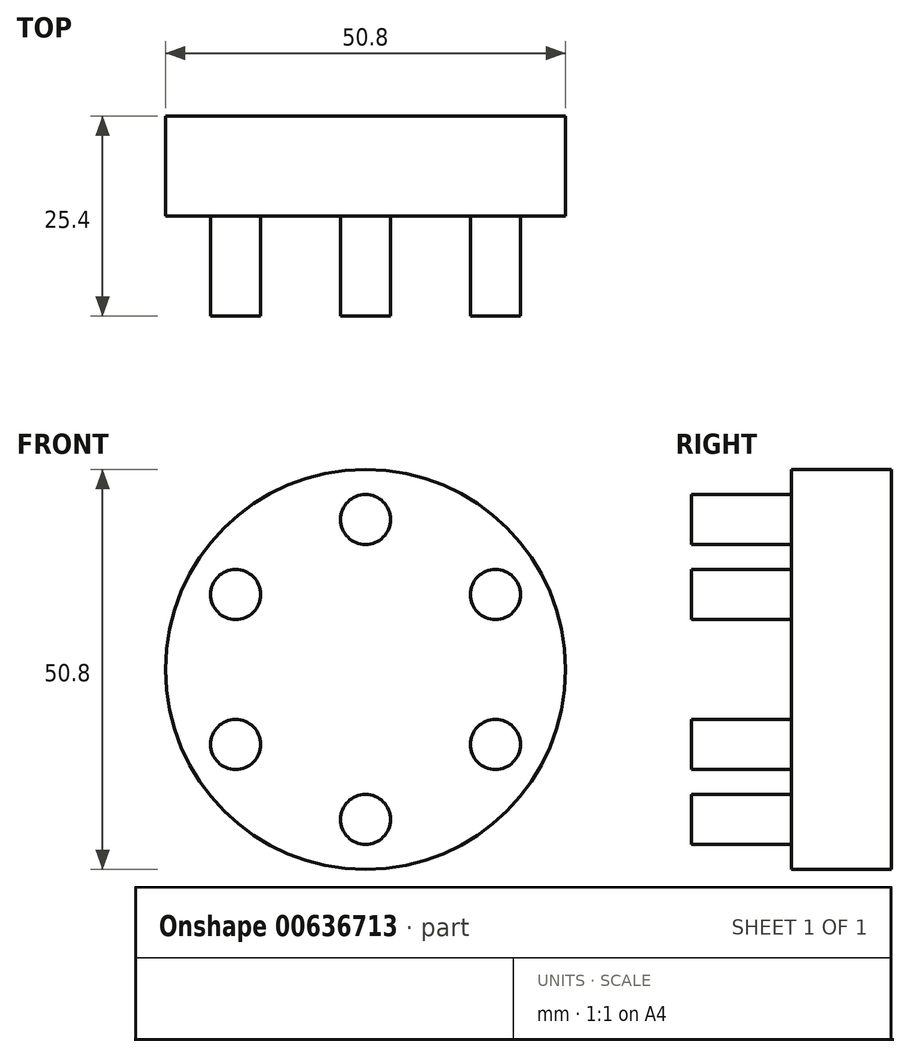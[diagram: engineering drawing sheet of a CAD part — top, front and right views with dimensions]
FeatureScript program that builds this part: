
annotation { "Feature Type Name" : "Feature", "Feature Type Description" : "" }
export const myFeature = defineFeature(function(context is Context, id is Id, definition is map)
    precondition{}
    {
        {
            var Q0;
            Q0=qCreatedBy(makeId("Front.planeOp"),FACE);
            var sketch = newSketch(context, id + "F0", { "sketchPlane" : qUnion([Q0])});
            skCircle(sketch, "E0", {"center": v(0, 0) * mm, "radius": 25.4 * mm});
            skLineSegment(sketch, "E1", {"start": v(0, 25.4) * mm, "end": v(0, 19.05) * mm, "construction": true});
            skCircle(sketch, "E2", {"center": v(0, 19.05) * mm, "radius": 3.18 * mm});
            skCircle(sketch, "E3.1.0", {"center": v(-16.5, 9.53) * mm, "radius": 3.18 * mm});
            skCircle(sketch, "E3.2.0", {"center": v(-16.5, -9.52) * mm, "radius": 3.18 * mm});
            skCircle(sketch, "E3.3.0", {"center": v(0, -19.05) * mm, "radius": 3.18 * mm});
            skCircle(sketch, "E3.4.0", {"center": v(16.5, -9.53) * mm, "radius": 3.18 * mm});
            skCircle(sketch, "E3.5.0", {"center": v(16.5, 9.53) * mm, "radius": 3.18 * mm});
            skSolve(sketch);
        }
        {
            var Q0;
            Q0=makeQuery(id+"F0.imprint","IMPRINT",FACE,{"disambiguationData":[TD([[makeQuery(id+"F0.imprint","IMPRINT",EDGE,{"derivedFrom":sQuery(id+"F0.wireOp",EDGE,"E0")}),1.0]])]});
            extrude(context, id + "F1", {"entities" : qUnion([Q0]), "depth" : 12.7 * mm, "offsetDistance" : 25.4 * mm});
        }
        {
            var Q0;
            Q0=makeQuery(id+"F0.imprint","IMPRINT",FACE,{"disambiguationData":[TD([[makeQuery(id+"F0.imprint","IMPRINT",EDGE,{"derivedFrom":sQuery(id+"F0.wireOp",EDGE,"E3.1.0")}),1.0]])]});
            var Q1;
            Q1=makeQuery(id+"F0.imprint","IMPRINT",FACE,{"disambiguationData":[TD([[makeQuery(id+"F0.imprint","IMPRINT",EDGE,{"derivedFrom":sQuery(id+"F0.wireOp",EDGE,"E2")}),1.0]])]});
            var Q2;
            Q2=makeQuery(id+"F0.imprint","IMPRINT",FACE,{"disambiguationData":[TD([[makeQuery(id+"F0.imprint","IMPRINT",EDGE,{"derivedFrom":sQuery(id+"F0.wireOp",EDGE,"E3.5.0")}),1.0]])]});
            var Q3;
            Q3=makeQuery(id+"F0.imprint","IMPRINT",FACE,{"disambiguationData":[TD([[makeQuery(id+"F0.imprint","IMPRINT",EDGE,{"derivedFrom":sQuery(id+"F0.wireOp",EDGE,"E3.4.0")}),1.0]])]});
            var Q4;
            Q4=makeQuery(id+"F0.imprint","IMPRINT",FACE,{"disambiguationData":[TD([[makeQuery(id+"F0.imprint","IMPRINT",EDGE,{"derivedFrom":sQuery(id+"F0.wireOp",EDGE,"E3.3.0")}),1.0]])]});
            var Q5;
            Q5=makeQuery(id+"F0.imprint","IMPRINT",FACE,{"disambiguationData":[TD([[makeQuery(id+"F0.imprint","IMPRINT",EDGE,{"derivedFrom":sQuery(id+"F0.wireOp",EDGE,"E3.2.0")}),1.0]])]});
            extrude(context, id + "F2", {"entities" : qUnion([Q0, Q1, Q2, Q3, Q4, Q5]), "operationType" : NewBodyOperationType.ADD, "depth" : 25.4 * mm, "offsetDistance" : 25.4 * mm});
        }
    });
